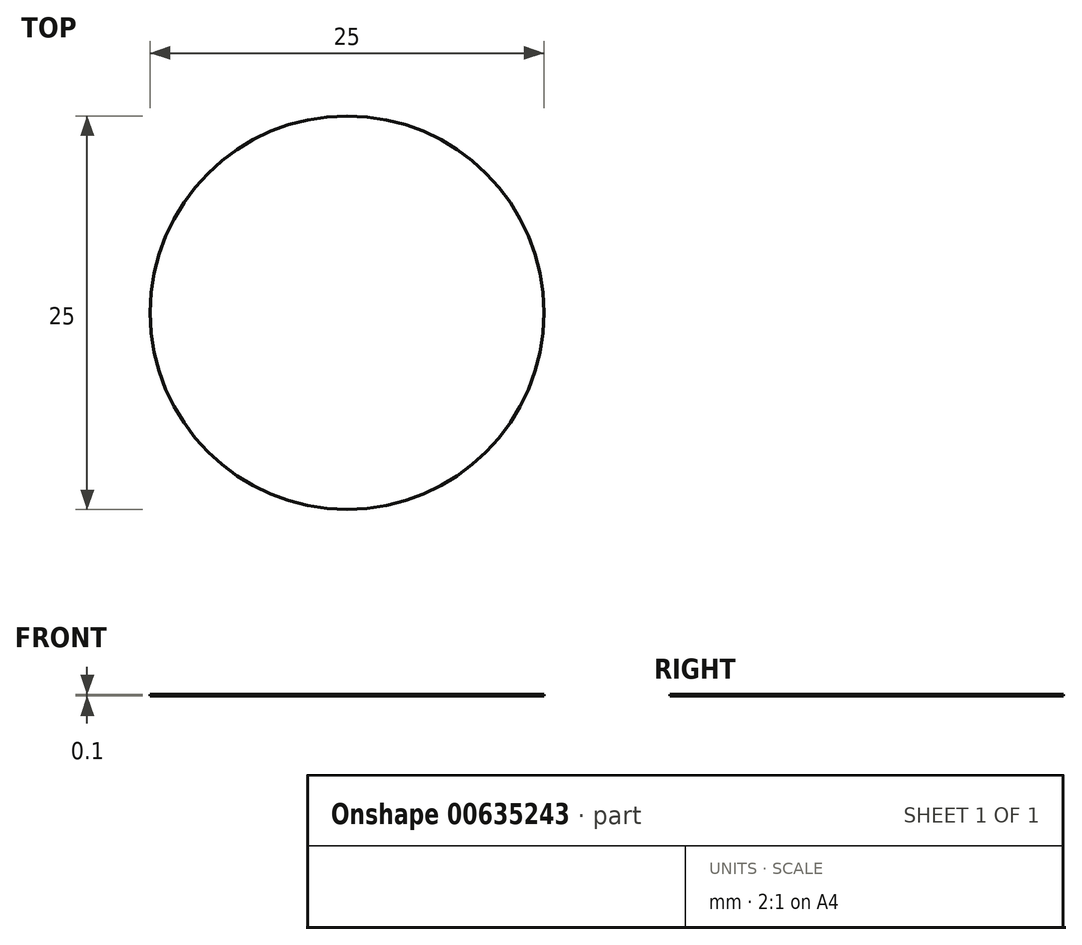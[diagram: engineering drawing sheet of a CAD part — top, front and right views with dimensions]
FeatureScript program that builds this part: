
annotation { "Feature Type Name" : "Feature", "Feature Type Description" : "" }
export const myFeature = defineFeature(function(context is Context, id is Id, definition is map)
    precondition{}
    {
        {
            var Q0;
            Q0=qCreatedBy(makeId("Top.planeOp"),FACE);
            var sketch = newSketch(context, id + "F0", { "sketchPlane" : qUnion([Q0])});
            skCircle(sketch, "E0", {"center": v(0, 0) * mm, "radius": 12.5 * mm});
            skSolve(sketch);
        }
        {
            var Q0;
            Q0=makeQuery(id+"F0.imprint","IMPRINT",FACE,{"disambiguationData":[TD([[makeQuery(id+"F0.imprint","IMPRINT",EDGE,{"derivedFrom":sQuery(id+"F0.wireOp",EDGE,"E0")}),1.0]])]});
            extrude(context, id + "F1", {"entities" : qUnion([Q0]), "depth" : 0.1 * mm, "offsetDistance" : 25 * mm});
        }
    });
